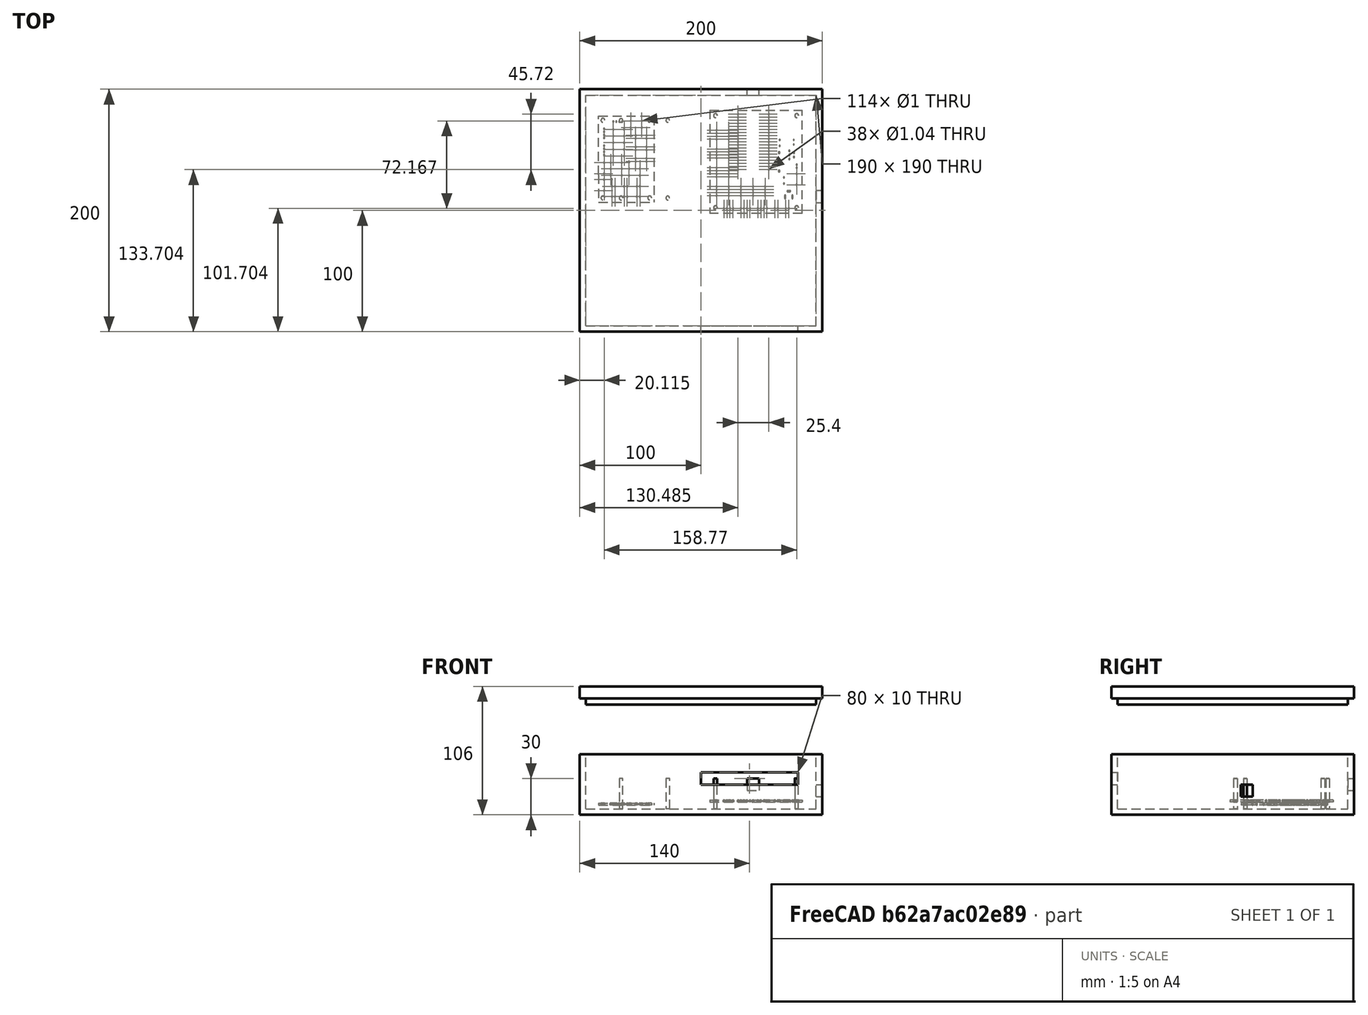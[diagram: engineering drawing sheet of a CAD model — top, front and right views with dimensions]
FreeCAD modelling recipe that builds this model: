
FCSTD DOCUMENT  (FreeCAD 0.21R33694 (Git))
Label: electronics_enclosure
License: All rights reserved
LicenseURL: https://en.wikipedia.org/wiki/All_rights_reserved
objects: Part::Cylinder×8, Part::Box×7, App::Part×6, Part::MultiFuse×3, PartDesign::CoordinateSystem×2, Part::Feature×2, Sketcher::SketchObject×2, Part::Cut×2
note: 26 computed .brp shape members not serialized (recipe doc carries the construction recipe); baked Part::Feature solids carry a one-line shape summary decoded from their .brp

FEATURE [PartDesign::CoordinateSystem] Local_CS_ebcb
  AttacherType = Attacher::AttachEngine3D
  MapMode = 2
  Support = -> [X_Axis001]
FEATURE [Part::Feature] Pcb_ebcb
  Placement = pos=(-66.3846,203.371,9.60288) rot=(0,0,1;0rad)
  shape: bbox 45.5 x 71 x 1.6 mm, 75 faces (baked)
FEATURE [Sketcher::SketchObject] PCB_Sketch_ebcb
  FullyConstrained = false
  sketch-geometry (5):
    g0: LineSegment StartX=82 StartY=-96.5 StartZ=0 EndX=127.5 EndY=-96.5 EndZ=0
    g1: LineSegment StartX=82 StartY=-74 StartZ=0 EndX=82 EndY=-96.5 EndZ=0
    g2: LineSegment StartX=82 StartY=-25.5 StartZ=0 EndX=127.5 EndY=-25.5 EndZ=0
    g3: LineSegment StartX=127.5 StartY=-25.5 StartZ=0 EndX=127.5 EndY=-96.5 EndZ=0
    g4: LineSegment StartX=82 StartY=-74 StartZ=0 EndX=82 EndY=-25.5 EndZ=0
  constraints (5):
    c: Coincident(g0,g1)
    c: Coincident(g1,g4)
    c: Coincident(g2,g4)
    c: Coincident(g0,g3)
    c: Coincident(g2,g3)
FEATURE [App::Part] Board_Geoms_ebcb
  Group = -> [Pcb_ebcb,PCB_Sketch_ebcb]
  Origin = -> Origin
  Placement = pos=(6.93612,-0.134552,0.200878) rot=(0,0,1;0rad)
FEATURE [App::Part] Step_Models_ebcb
  Origin = -> Origin002
FEATURE [App::Part] Board_ebcb  label="ir_sensor"
  Group = -> [Local_CS_ebcb,Board_Geoms_ebcb,Step_Models_ebcb]
  Origin = -> Origin001
  Placement = pos=(8,0,0) rot=(0,0,1;0rad)
FEATURE [PartDesign::CoordinateSystem] Local_CS_b27c
  AttacherType = Attacher::AttachEngine3D
  MapMode = 2
  Support = -> [X_Axis004]
FEATURE [Part::Feature] Pcb_b27c
  Placement = pos=(-27.615,242.704,12.0679) rot=(0,0,1;0rad)
  shape: bbox 76 x 85 x 1.6 mm, 143 faces (baked)
FEATURE [Sketcher::SketchObject] PCB_Sketch_b27c
  FullyConstrained = false
  sketch-geometry (4):
    g0: LineSegment StartX=211 StartY=-145 StartZ=0 EndX=211 EndY=-60 EndZ=0
    g1: LineSegment StartX=135 StartY=-60 StartZ=0 EndX=135 EndY=-145 EndZ=0
    g2: LineSegment StartX=211 StartY=-145 StartZ=0 EndX=135 EndY=-145 EndZ=0
    g3: LineSegment StartX=135 StartY=-60 StartZ=0 EndX=211 EndY=-60 EndZ=0
  constraints (4):
    c: Coincident(g1,g2)
    c: Coincident(g1,g3)
    c: Coincident(g0,g2)
    c: Coincident(g0,g3)
FEATURE [App::Part] Board_Geoms_b27c
  Group = -> [Pcb_b27c,PCB_Sketch_b27c]
  Origin = -> Origin003
FEATURE [App::Part] Step_Models_b27c
  Origin = -> Origin005
FEATURE [App::Part] Board_b27c  label="beehive"
  Group = -> [Local_CS_b27c,Board_Geoms_b27c,Step_Models_b27c]
  Origin = -> Origin004
FEATURE [Part::Box] Box  label="Cube"
  AttacherType = Attacher::AttachEngine3D
  Height = 50
  Length = 200
  Width = 200
FEATURE [Part::Box] Box001  label="Cube001"
  AttacherType = Attacher::AttachEngine3D
  Height = 45
  Length = 190
  Placement = pos=(5,5,5) rot=(0,0,1;0rad)
  Width = 190
FEATURE [Part::Cut] Cut
  Base = -> Box
  Tool = -> Box001
FEATURE [Part::Cylinder] Cylinder
  Angle = 360
  AttacherType = Attacher::AttachEngine3D
  FirstAngle = 0
  Height = 30
  Placement = pos=(111.89,102.19,0) rot=(0,0,1;0rad)
  Radius = 1.5
  SecondAngle = 0
FEATURE [Part::Cylinder] Cylinder001
  Angle = 360
  AttacherType = Attacher::AttachEngine3D
  FirstAngle = 0
  Height = 30
  Placement = pos=(111.89,178.19,0) rot=(0,0,1;0rad)
  Radius = 1.5
  SecondAngle = 0
FEATURE [Part::Cylinder] Cylinder002
  Angle = 360
  AttacherType = Attacher::AttachEngine3D
  FirstAngle = 0
  Height = 30
  Placement = pos=(178.89,178.19,0) rot=(0,0,1;0rad)
  Radius = 1.5
  SecondAngle = 0
FEATURE [Part::Cylinder] Cylinder003
  Angle = 360
  AttacherType = Attacher::AttachEngine3D
  FirstAngle = 0
  Height = 30
  Placement = pos=(178.89,102.19,0) rot=(0,0,1;0rad)
  Radius = 1.5
  SecondAngle = 0
FEATURE [Part::Cylinder] Cylinder004
  Angle = 360
  AttacherType = Attacher::AttachEngine3D
  FirstAngle = 0
  Height = 30
  Placement = pos=(72.56,110.24,0) rot=(0,0,1;0rad)
  Radius = 1.5
  SecondAngle = 0
FEATURE [Part::Cylinder] Cylinder005
  Angle = 360
  AttacherType = Attacher::AttachEngine3D
  FirstAngle = 0
  Height = 30
  Placement = pos=(72.56,174.24,0) rot=(0,0,1;0rad)
  Radius = 1.5
  SecondAngle = 0
FEATURE [Part::Cylinder] Cylinder006
  Angle = 360
  AttacherType = Attacher::AttachEngine3D
  FirstAngle = 0
  Height = 30
  Placement = pos=(34.06,174.24,0) rot=(0,0,1;0rad)
  Radius = 1.5
  SecondAngle = 0
FEATURE [Part::Cylinder] Cylinder007
  Angle = 360
  AttacherType = Attacher::AttachEngine3D
  FirstAngle = 0
  Height = 30
  Placement = pos=(34.06,110.24,0) rot=(0,0,1;0rad)
  Radius = 1.5
  SecondAngle = 0
FEATURE [Part::Box] Box002  label="Cube002"
  AttacherType = Attacher::AttachEngine3D
  Height = 10
  Length = 10
  Placement = pos=(138,190.5,20) rot=(0,0,1;0rad)
  Width = 10
FEATURE [Part::Box] Box003  label="Cube003"
  AttacherType = Attacher::AttachEngine3D
  Height = 10
  Length = 10
  Placement = pos=(191,106.5,15) rot=(0,0,1;0rad)
  Width = 10
FEATURE [Part::Box] Box004  label="Cube004"
  AttacherType = Attacher::AttachEngine3D
  Height = 10
  Length = 80
  Placement = pos=(100,-1,25) rot=(0,0,1;0rad)
  Width = 10
FEATURE [Part::MultiFuse] Fusion
  Shapes = -> [Box002,Box003,Box004]
FEATURE [Part::Cut] Cut001
  Base = -> Cut
  Tool = -> Fusion
FEATURE [Part::MultiFuse] Fusion001  label="box_bottom"
  Shapes = -> [Cut001,Cylinder007,Cylinder006,Cylinder005,Cylinder004,Cylinder003,Cylinder002,Cylinder001,Cylinder]
FEATURE [Part::Box] Box005  label="Cube005"
  AttacherType = Attacher::AttachEngine3D
  Height = 10
  Length = 200
  Placement = pos=(0,0,96) rot=(0,0,1;0rad)
  Width = 200
FEATURE [Part::Box] Box006  label="Cube006"
  AttacherType = Attacher::AttachEngine3D
  Height = 15
  Length = 190
  Placement = pos=(5,5,91) rot=(0,0,1;0rad)
  Width = 190
FEATURE [Part::MultiFuse] Fusion002  label="lid"
  Shapes = -> [Box005,Box006]
